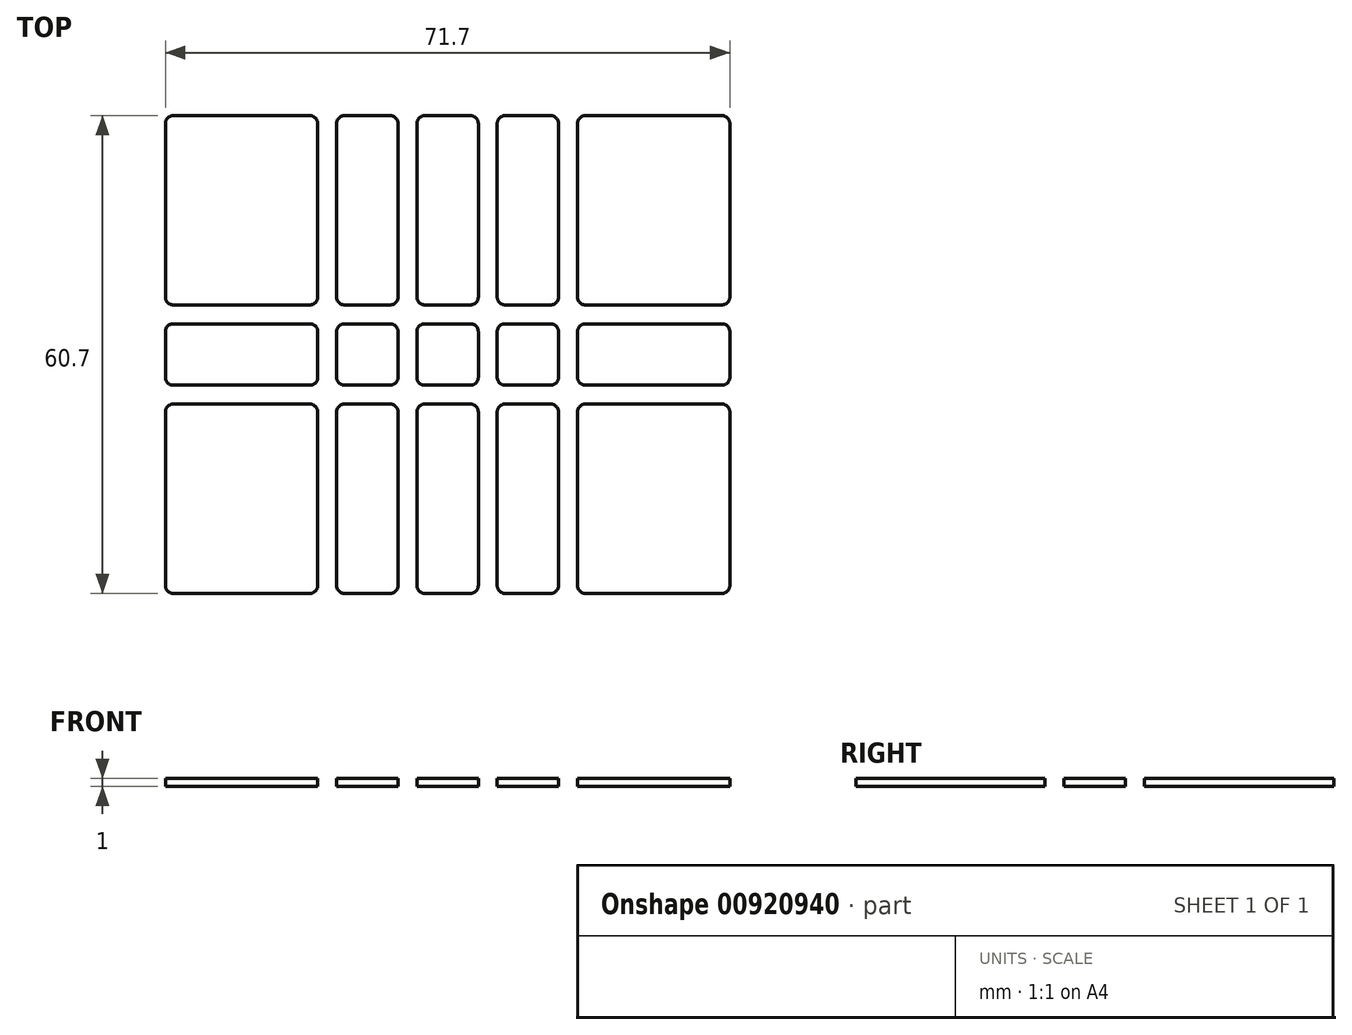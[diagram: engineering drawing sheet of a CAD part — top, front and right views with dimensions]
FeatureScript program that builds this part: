
annotation { "Feature Type Name" : "Feature", "Feature Type Description" : "" }
export const myFeature = defineFeature(function(context is Context, id is Id, definition is map)
    precondition{}
    {
        {
            var Q0;
            Q0=qCreatedBy(makeId("Top.planeOp"),FACE);
            var sketch = newSketch(context, id + "F0", { "sketchPlane" : qUnion([Q0])});
            skLineSegment(sketch, "E0.bottom", {"start": v(38.85, 33.35) * mm, "end": v(-38.85, 33.35) * mm, "construction": true});
            skLineSegment(sketch, "E0.top", {"start": v(38.85, -33.35) * mm, "end": v(-38.85, -33.35) * mm, "construction": true});
            skLineSegment(sketch, "E0.left", {"start": v(38.85, 33.35) * mm, "end": v(38.85, -33.35) * mm, "construction": true});
            skLineSegment(sketch, "E0.right", {"start": v(-38.85, 33.35) * mm, "end": v(-38.85, -33.35) * mm, "construction": true});
            skLineSegment(sketch, "E1", {"start": v(0, 0) * mm, "end": v(0, -33.35) * mm, "construction": true});
            skLineSegment(sketch, "E2", {"start": v(-5.1, 0) * mm, "end": v(-5.1, -33.35) * mm, "construction": true});
            skLineSegment(sketch, "E3", {"start": v(-15.3, 0) * mm, "end": v(-15.3, -33.35) * mm, "construction": true});
            skLineSegment(sketch, "E4.MirrorCS", {"start": v(5.1, 0) * mm, "end": v(5.1, -33.35) * mm, "construction": true});
            skLineSegment(sketch, "E5", {"start": v(0, 0) * mm, "end": v(-38.85, 0) * mm, "construction": true});
            skLineSegment(sketch, "E6", {"start": v(0, -5.1) * mm, "end": v(-38.85, -5.1) * mm, "construction": true});
            skLineSegment(sketch, "E7.MirrorCS", {"start": v(0, 5.1) * mm, "end": v(-38.85, 5.1) * mm, "construction": true});
            skLineSegment(sketch, "E8.bottom", {"start": v(-34.85, -6.3) * mm, "end": v(-17.5, -6.3) * mm});
            skLineSegment(sketch, "E8.top", {"start": v(-34.85, -30.35) * mm, "end": v(-17.5, -30.35) * mm});
            skLineSegment(sketch, "E8.left", {"start": v(-35.85, -7.3) * mm, "end": v(-35.85, -29.35) * mm});
            skLineSegment(sketch, "E8.right", {"start": v(-16.5, -7.3) * mm, "end": v(-16.5, -29.35) * mm});
            skLineSegment(sketch, "E9.bottom", {"start": v(-13.1, -6.3) * mm, "end": v(-7.3, -6.3) * mm});
            skLineSegment(sketch, "E9.top", {"start": v(-13.1, -30.35) * mm, "end": v(-7.3, -30.35) * mm});
            skLineSegment(sketch, "E9.left", {"start": v(-14.1, -7.3) * mm, "end": v(-14.1, -29.35) * mm});
            skLineSegment(sketch, "E9.right", {"start": v(-6.3, -7.3) * mm, "end": v(-6.3, -29.35) * mm});
            skLineSegment(sketch, "E10.bottom", {"start": v(-2.9, -6.3) * mm, "end": v(2.9, -6.3) * mm});
            skLineSegment(sketch, "E10.top", {"start": v(-2.9, -30.35) * mm, "end": v(2.9, -30.35) * mm});
            skLineSegment(sketch, "E10.left", {"start": v(-3.9, -7.3) * mm, "end": v(-3.9, -29.35) * mm});
            skLineSegment(sketch, "E10.right", {"start": v(3.9, -7.3) * mm, "end": v(3.9, -29.35) * mm});
            skLineSegment(sketch, "E11.bottom", {"start": v(-34.85, 3.9) * mm, "end": v(-17.5, 3.9) * mm});
            skLineSegment(sketch, "E11.top", {"start": v(-34.85, -3.9) * mm, "end": v(-17.5, -3.9) * mm});
            skLineSegment(sketch, "E11.left", {"start": v(-35.85, 2.9) * mm, "end": v(-35.85, -2.9) * mm});
            skLineSegment(sketch, "E11.right", {"start": v(-16.5, 2.9) * mm, "end": v(-16.5, -2.9) * mm});
            skLineSegment(sketch, "E12.bottom", {"start": v(-13.1, 3.9) * mm, "end": v(-7.3, 3.9) * mm});
            skLineSegment(sketch, "E12.top", {"start": v(-13.1, -3.9) * mm, "end": v(-7.3, -3.9) * mm});
            skLineSegment(sketch, "E12.left", {"start": v(-14.1, 2.9) * mm, "end": v(-14.1, -2.9) * mm});
            skLineSegment(sketch, "E12.right", {"start": v(-6.3, 2.9) * mm, "end": v(-6.3, -2.9) * mm});
            skLineSegment(sketch, "E13.bottom", {"start": v(-2.9, 3.9) * mm, "end": v(2.9, 3.9) * mm});
            skLineSegment(sketch, "E13.top", {"start": v(-2.9, -3.9) * mm, "end": v(2.9, -3.9) * mm});
            skLineSegment(sketch, "E13.left", {"start": v(-3.9, 2.9) * mm, "end": v(-3.9, -2.9) * mm});
            skLineSegment(sketch, "E13.right", {"start": v(3.9, 2.9) * mm, "end": v(3.9, -2.9) * mm});
            skPoint(sketch, "E14.visualSharp", {"position": v(-35.85, -30.35) * mm});
            skArc(sketch, "E14.filletArc", {"start": v(-35.85, -29.35) * mm, "mid": v(-35.56, -30.06) * mm, "end": v(-34.85, -30.35) * mm});
            skPoint(sketch, "E15.visualSharp", {"position": v(-16.5, -30.35) * mm});
            skArc(sketch, "E15.filletArc", {"start": v(-17.5, -30.35) * mm, "mid": v(-16.8, -30.06) * mm, "end": v(-16.5, -29.35) * mm});
            skPoint(sketch, "E16.visualSharp", {"position": v(-14.1, -30.35) * mm});
            skArc(sketch, "E16.filletArc", {"start": v(-14.1, -29.35) * mm, "mid": v(-13.8, -30.06) * mm, "end": v(-13.1, -30.35) * mm});
            skPoint(sketch, "E17.visualSharp", {"position": v(-6.3, -30.35) * mm});
            skArc(sketch, "E17.filletArc", {"start": v(-7.3, -30.35) * mm, "mid": v(-6.6, -30.06) * mm, "end": v(-6.3, -29.35) * mm});
            skPoint(sketch, "E18.visualSharp", {"position": v(-3.9, -30.35) * mm});
            skArc(sketch, "E18.filletArc", {"start": v(-3.9, -29.35) * mm, "mid": v(-3.6, -30.06) * mm, "end": v(-2.9, -30.35) * mm});
            skPoint(sketch, "E19.visualSharp", {"position": v(3.9, -30.35) * mm});
            skArc(sketch, "E19.filletArc", {"start": v(2.9, -30.35) * mm, "mid": v(3.6, -30.06) * mm, "end": v(3.9, -29.35) * mm});
            skPoint(sketch, "E20.visualSharp", {"position": v(3.9, -6.3) * mm});
            skArc(sketch, "E20.filletArc", {"start": v(3.9, -7.3) * mm, "mid": v(3.6, -6.6) * mm, "end": v(2.9, -6.3) * mm});
            skPoint(sketch, "E21.visualSharp", {"position": v(-3.9, -6.3) * mm});
            skArc(sketch, "E21.filletArc", {"start": v(-2.9, -6.3) * mm, "mid": v(-3.6, -6.6) * mm, "end": v(-3.9, -7.3) * mm});
            skPoint(sketch, "E22.visualSharp", {"position": v(-6.3, -6.3) * mm});
            skArc(sketch, "E22.filletArc", {"start": v(-6.3, -7.3) * mm, "mid": v(-6.6, -6.6) * mm, "end": v(-7.3, -6.3) * mm});
            skPoint(sketch, "E23.visualSharp", {"position": v(-14.1, -6.3) * mm});
            skArc(sketch, "E23.filletArc", {"start": v(-13.1, -6.3) * mm, "mid": v(-13.8, -6.6) * mm, "end": v(-14.1, -7.3) * mm});
            skPoint(sketch, "E24.visualSharp", {"position": v(-16.5, -6.3) * mm});
            skArc(sketch, "E24.filletArc", {"start": v(-16.5, -7.3) * mm, "mid": v(-16.8, -6.6) * mm, "end": v(-17.5, -6.3) * mm});
            skPoint(sketch, "E25.visualSharp", {"position": v(-35.85, -6.3) * mm});
            skArc(sketch, "E25.filletArc", {"start": v(-34.85, -6.3) * mm, "mid": v(-35.56, -6.6) * mm, "end": v(-35.85, -7.3) * mm});
            skPoint(sketch, "E26.visualSharp", {"position": v(-35.85, -3.9) * mm});
            skArc(sketch, "E26.filletArc", {"start": v(-35.85, -2.9) * mm, "mid": v(-35.56, -3.6) * mm, "end": v(-34.85, -3.9) * mm});
            skPoint(sketch, "E27.visualSharp", {"position": v(-16.5, -3.9) * mm});
            skArc(sketch, "E27.filletArc", {"start": v(-17.5, -3.9) * mm, "mid": v(-16.8, -3.6) * mm, "end": v(-16.5, -2.9) * mm});
            skPoint(sketch, "E28.visualSharp", {"position": v(-14.1, -3.9) * mm});
            skArc(sketch, "E28.filletArc", {"start": v(-14.1, -2.9) * mm, "mid": v(-13.8, -3.6) * mm, "end": v(-13.1, -3.9) * mm});
            skPoint(sketch, "E29.visualSharp", {"position": v(-6.3, -3.9) * mm});
            skArc(sketch, "E29.filletArc", {"start": v(-7.3, -3.9) * mm, "mid": v(-6.6, -3.6) * mm, "end": v(-6.3, -2.9) * mm});
            skPoint(sketch, "E30.visualSharp", {"position": v(-3.9, -3.9) * mm});
            skArc(sketch, "E30.filletArc", {"start": v(-3.9, -2.9) * mm, "mid": v(-3.6, -3.6) * mm, "end": v(-2.9, -3.9) * mm});
            skPoint(sketch, "E31.visualSharp", {"position": v(3.9, -3.9) * mm});
            skArc(sketch, "E31.filletArc", {"start": v(2.9, -3.9) * mm, "mid": v(3.6, -3.6) * mm, "end": v(3.9, -2.9) * mm});
            skPoint(sketch, "E32.visualSharp", {"position": v(3.9, 3.9) * mm});
            skArc(sketch, "E32.filletArc", {"start": v(3.9, 2.9) * mm, "mid": v(3.6, 3.6) * mm, "end": v(2.9, 3.9) * mm});
            skPoint(sketch, "E33.visualSharp", {"position": v(-3.9, 3.9) * mm});
            skArc(sketch, "E33.filletArc", {"start": v(-2.9, 3.9) * mm, "mid": v(-3.6, 3.6) * mm, "end": v(-3.9, 2.9) * mm});
            skPoint(sketch, "E34.visualSharp", {"position": v(-6.3, 3.9) * mm});
            skArc(sketch, "E34.filletArc", {"start": v(-6.3, 2.9) * mm, "mid": v(-6.6, 3.6) * mm, "end": v(-7.3, 3.9) * mm});
            skPoint(sketch, "E35.visualSharp", {"position": v(-14.1, 3.9) * mm});
            skArc(sketch, "E35.filletArc", {"start": v(-13.1, 3.9) * mm, "mid": v(-13.8, 3.6) * mm, "end": v(-14.1, 2.9) * mm});
            skPoint(sketch, "E36.visualSharp", {"position": v(-16.5, 3.9) * mm});
            skArc(sketch, "E36.filletArc", {"start": v(-16.5, 2.9) * mm, "mid": v(-16.8, 3.6) * mm, "end": v(-17.5, 3.9) * mm});
            skPoint(sketch, "E37.visualSharp", {"position": v(-35.85, 3.9) * mm});
            skArc(sketch, "E37.filletArc", {"start": v(-34.85, 3.9) * mm, "mid": v(-35.56, 3.6) * mm, "end": v(-35.85, 2.9) * mm});
            skSolve(sketch);
        }
        {
            var Q0;
            Q0=qSketchRegion(id+"F0",true);
            extrude(context, id + "F1", {"entities" : qUnion([Q0]), "depth" : 1 * mm, "offsetDistance" : 25 * mm});
        }
        {
            var Q0;
            Q0=makeQuery(id+"F1.opExtrude","SWEPT_BODY",BODY,{"disambiguationData":[OSD([sQuery(id+"F0.wireOp",EDGE,"E8.bottom"),sQuery(id+"F0.wireOp",EDGE,"E8.top"),sQuery(id+"F0.wireOp",EDGE,"E8.left"),sQuery(id+"F0.wireOp",EDGE,"E8.right"),sQuery(id+"F0.wireOp",EDGE,"E14.filletArc"),sQuery(id+"F0.wireOp",EDGE,"E15.filletArc"),sQuery(id+"F0.wireOp",EDGE,"E24.filletArc"),sQuery(id+"F0.wireOp",EDGE,"E25.filletArc")])]});
            var Q1;
            Q1=makeQuery(id+"F1.opExtrude","SWEPT_BODY",BODY,{"disambiguationData":[OSD([sQuery(id+"F0.wireOp",EDGE,"aZ2vjbnt-IJ6G-xpWL-Nf7q-FU5Z6CCyIqXy.bottom"),sQuery(id+"F0.wireOp",EDGE,"aZ2vjbnt-IJ6G-xpWL-Nf7q-FU5Z6CCyIqXy.top"),sQuery(id+"F0.wireOp",EDGE,"aZ2vjbnt-IJ6G-xpWL-Nf7q-FU5Z6CCyIqXy.left"),sQuery(id+"F0.wireOp",EDGE,"aZ2vjbnt-IJ6G-xpWL-Nf7q-FU5Z6CCyIqXy.right"),sQuery(id+"F0.wireOp",EDGE,"be82f8eb-51d7-4f74-a791-70583ad3d47f.filletArc"),sQuery(id+"F0.wireOp",EDGE,"28ddf411-c316-4165-98ff-05157f18c76e.filletArc"),sQuery(id+"F0.wireOp",EDGE,"964d3b43-0fab-4451-8acc-3eb9fe7dbb03.filletArc"),sQuery(id+"F0.wireOp",EDGE,"ebbf5183-c798-4928-8d37-be99f6c13325.filletArc")])]});
            var Q2;
            Q2=makeQuery(id+"F1.opExtrude","SWEPT_BODY",BODY,{"disambiguationData":[OSD([sQuery(id+"F0.wireOp",EDGE,"E9.bottom"),sQuery(id+"F0.wireOp",EDGE,"E9.top"),sQuery(id+"F0.wireOp",EDGE,"E9.left"),sQuery(id+"F0.wireOp",EDGE,"E9.right"),sQuery(id+"F0.wireOp",EDGE,"E16.filletArc"),sQuery(id+"F0.wireOp",EDGE,"E17.filletArc"),sQuery(id+"F0.wireOp",EDGE,"E22.filletArc"),sQuery(id+"F0.wireOp",EDGE,"E23.filletArc")])]});
            var Q3;
            Q3=makeQuery(id+"F1.opExtrude","SWEPT_BODY",BODY,{"disambiguationData":[OSD([sQuery(id+"F0.wireOp",EDGE,"E10.bottom"),sQuery(id+"F0.wireOp",EDGE,"E10.top"),sQuery(id+"F0.wireOp",EDGE,"E10.left"),sQuery(id+"F0.wireOp",EDGE,"E10.right"),sQuery(id+"F0.wireOp",EDGE,"E18.filletArc"),sQuery(id+"F0.wireOp",EDGE,"E19.filletArc"),sQuery(id+"F0.wireOp",EDGE,"E20.filletArc"),sQuery(id+"F0.wireOp",EDGE,"E21.filletArc")])]});
            var Q4;
            Q4=qCreatedBy(makeId("Front.planeOp"),FACE);
            mirror(context, id + "F2", {"entities" : qUnion([Q0, Q1, Q2, Q3]), "mirrorPlane" : qUnion([Q4])});
        }
        {
            var Q0;
            Q0=makeQuery(id+"F2.opPattern","COPY",BODY,{"derivedFrom":makeQuery(id+"F1.opExtrude","SWEPT_BODY",BODY,{"disambiguationData":[OSD([sQuery(id+"F0.wireOp",EDGE,"E8.bottom"),sQuery(id+"F0.wireOp",EDGE,"E8.top"),sQuery(id+"F0.wireOp",EDGE,"E8.left"),sQuery(id+"F0.wireOp",EDGE,"E8.right"),sQuery(id+"F0.wireOp",EDGE,"E14.filletArc"),sQuery(id+"F0.wireOp",EDGE,"E15.filletArc"),sQuery(id+"F0.wireOp",EDGE,"E24.filletArc"),sQuery(id+"F0.wireOp",EDGE,"E25.filletArc")])]}),"instanceName":"1"});
            var Q1;
            Q1=makeQuery(id+"F2.opPattern","COPY",BODY,{"derivedFrom":makeQuery(id+"F1.opExtrude","SWEPT_BODY",BODY,{"disambiguationData":[OSD([sQuery(id+"F0.wireOp",EDGE,"aZ2vjbnt-IJ6G-xpWL-Nf7q-FU5Z6CCyIqXy.bottom"),sQuery(id+"F0.wireOp",EDGE,"aZ2vjbnt-IJ6G-xpWL-Nf7q-FU5Z6CCyIqXy.top"),sQuery(id+"F0.wireOp",EDGE,"aZ2vjbnt-IJ6G-xpWL-Nf7q-FU5Z6CCyIqXy.left"),sQuery(id+"F0.wireOp",EDGE,"aZ2vjbnt-IJ6G-xpWL-Nf7q-FU5Z6CCyIqXy.right"),sQuery(id+"F0.wireOp",EDGE,"be82f8eb-51d7-4f74-a791-70583ad3d47f.filletArc"),sQuery(id+"F0.wireOp",EDGE,"28ddf411-c316-4165-98ff-05157f18c76e.filletArc"),sQuery(id+"F0.wireOp",EDGE,"964d3b43-0fab-4451-8acc-3eb9fe7dbb03.filletArc"),sQuery(id+"F0.wireOp",EDGE,"ebbf5183-c798-4928-8d37-be99f6c13325.filletArc")])]}),"instanceName":"1"});
            var Q2;
            Q2=makeQuery(id+"F2.opPattern","COPY",BODY,{"derivedFrom":makeQuery(id+"F1.opExtrude","SWEPT_BODY",BODY,{"disambiguationData":[OSD([sQuery(id+"F0.wireOp",EDGE,"E9.bottom"),sQuery(id+"F0.wireOp",EDGE,"E9.top"),sQuery(id+"F0.wireOp",EDGE,"E9.left"),sQuery(id+"F0.wireOp",EDGE,"E9.right"),sQuery(id+"F0.wireOp",EDGE,"E16.filletArc"),sQuery(id+"F0.wireOp",EDGE,"E17.filletArc"),sQuery(id+"F0.wireOp",EDGE,"E22.filletArc"),sQuery(id+"F0.wireOp",EDGE,"E23.filletArc")])]}),"instanceName":"1"});
            var Q3;
            Q3=makeQuery(id+"F1.opExtrude","SWEPT_BODY",BODY,{"disambiguationData":[OSD([sQuery(id+"F0.wireOp",EDGE,"E12.bottom"),sQuery(id+"F0.wireOp",EDGE,"E12.top"),sQuery(id+"F0.wireOp",EDGE,"E12.left"),sQuery(id+"F0.wireOp",EDGE,"E12.right"),sQuery(id+"F0.wireOp",EDGE,"E28.filletArc"),sQuery(id+"F0.wireOp",EDGE,"E29.filletArc"),sQuery(id+"F0.wireOp",EDGE,"E34.filletArc"),sQuery(id+"F0.wireOp",EDGE,"E35.filletArc")])]});
            var Q4;
            Q4=makeQuery(id+"F1.opExtrude","SWEPT_BODY",BODY,{"disambiguationData":[OSD([sQuery(id+"F0.wireOp",EDGE,"8kwTGaSX-Ztku-dDTE-NIVn-plMZdAMdB52H.bottom"),sQuery(id+"F0.wireOp",EDGE,"8kwTGaSX-Ztku-dDTE-NIVn-plMZdAMdB52H.top"),sQuery(id+"F0.wireOp",EDGE,"8kwTGaSX-Ztku-dDTE-NIVn-plMZdAMdB52H.left"),sQuery(id+"F0.wireOp",EDGE,"8kwTGaSX-Ztku-dDTE-NIVn-plMZdAMdB52H.right"),sQuery(id+"F0.wireOp",EDGE,"27b70b49-23fa-4e29-aec9-036afc62a633.filletArc"),sQuery(id+"F0.wireOp",EDGE,"9138238a-beda-414c-9f45-198a131c761b.filletArc"),sQuery(id+"F0.wireOp",EDGE,"d01eb7d2-15b3-4fab-b4be-8801cad3b42d.filletArc"),sQuery(id+"F0.wireOp",EDGE,"d9b32b40-8166-495a-b5a2-4000195e6c02.filletArc")])]});
            var Q5;
            Q5=makeQuery(id+"F1.opExtrude","SWEPT_BODY",BODY,{"disambiguationData":[OSD([sQuery(id+"F0.wireOp",EDGE,"E11.bottom"),sQuery(id+"F0.wireOp",EDGE,"E11.top"),sQuery(id+"F0.wireOp",EDGE,"E11.left"),sQuery(id+"F0.wireOp",EDGE,"E11.right"),sQuery(id+"F0.wireOp",EDGE,"E26.filletArc"),sQuery(id+"F0.wireOp",EDGE,"E27.filletArc"),sQuery(id+"F0.wireOp",EDGE,"E36.filletArc"),sQuery(id+"F0.wireOp",EDGE,"E37.filletArc")])]});
            var Q6;
            Q6=makeQuery(id+"F1.opExtrude","SWEPT_BODY",BODY,{"disambiguationData":[OSD([sQuery(id+"F0.wireOp",EDGE,"E8.bottom"),sQuery(id+"F0.wireOp",EDGE,"E8.top"),sQuery(id+"F0.wireOp",EDGE,"E8.left"),sQuery(id+"F0.wireOp",EDGE,"E8.right"),sQuery(id+"F0.wireOp",EDGE,"E14.filletArc"),sQuery(id+"F0.wireOp",EDGE,"E15.filletArc"),sQuery(id+"F0.wireOp",EDGE,"E24.filletArc"),sQuery(id+"F0.wireOp",EDGE,"E25.filletArc")])]});
            var Q7;
            Q7=makeQuery(id+"F1.opExtrude","SWEPT_BODY",BODY,{"disambiguationData":[OSD([sQuery(id+"F0.wireOp",EDGE,"aZ2vjbnt-IJ6G-xpWL-Nf7q-FU5Z6CCyIqXy.bottom"),sQuery(id+"F0.wireOp",EDGE,"aZ2vjbnt-IJ6G-xpWL-Nf7q-FU5Z6CCyIqXy.top"),sQuery(id+"F0.wireOp",EDGE,"aZ2vjbnt-IJ6G-xpWL-Nf7q-FU5Z6CCyIqXy.left"),sQuery(id+"F0.wireOp",EDGE,"aZ2vjbnt-IJ6G-xpWL-Nf7q-FU5Z6CCyIqXy.right"),sQuery(id+"F0.wireOp",EDGE,"be82f8eb-51d7-4f74-a791-70583ad3d47f.filletArc"),sQuery(id+"F0.wireOp",EDGE,"28ddf411-c316-4165-98ff-05157f18c76e.filletArc"),sQuery(id+"F0.wireOp",EDGE,"964d3b43-0fab-4451-8acc-3eb9fe7dbb03.filletArc"),sQuery(id+"F0.wireOp",EDGE,"ebbf5183-c798-4928-8d37-be99f6c13325.filletArc")])]});
            var Q8;
            Q8=makeQuery(id+"F1.opExtrude","SWEPT_BODY",BODY,{"disambiguationData":[OSD([sQuery(id+"F0.wireOp",EDGE,"E9.bottom"),sQuery(id+"F0.wireOp",EDGE,"E9.top"),sQuery(id+"F0.wireOp",EDGE,"E9.left"),sQuery(id+"F0.wireOp",EDGE,"E9.right"),sQuery(id+"F0.wireOp",EDGE,"E16.filletArc"),sQuery(id+"F0.wireOp",EDGE,"E17.filletArc"),sQuery(id+"F0.wireOp",EDGE,"E22.filletArc"),sQuery(id+"F0.wireOp",EDGE,"E23.filletArc")])]});
            var Q9;
            Q9=qCreatedBy(makeId("Right.planeOp"),FACE);
            mirror(context, id + "F3", {"entities" : qUnion([Q0, Q1, Q2, Q3, Q4, Q5, Q6, Q7, Q8]), "mirrorPlane" : qUnion([Q9])});
        }
    });
